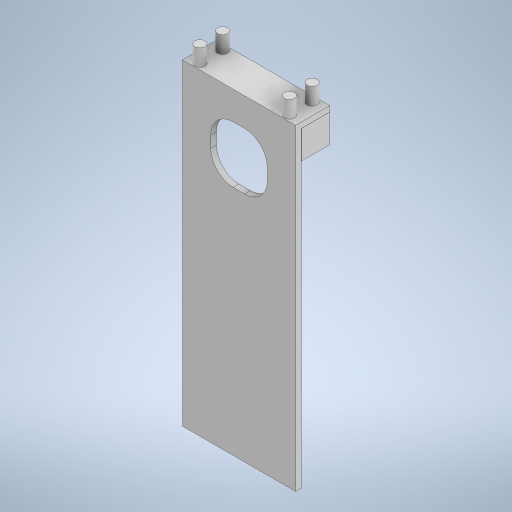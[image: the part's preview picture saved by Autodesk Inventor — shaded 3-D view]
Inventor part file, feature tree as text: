
AUTODESK INVENTOR PART (.ipt)
format: ipt  version: 2023 (Build 270158000, 158)  size: 316,928 bytes
history: native  units: mm
features: extrude x8, sketch x8
ambient origin geometry x8: Origin, YZ Plane, XZ Plane, XY Plane, X Axis, Y Axis, Z Axis, Center Point
bodies: Solid1 (feature_tree)
feature tree (16):
  extrude  "Extrusion1"  Depth=100.0mm
  extrude  "Extrusion6"  Depth=50.0mm
  sketch  "Sketch15"  dims[d22=50.0mm d23=20.0mm]
  sketch  "Sketch16"  dims[d24=5.0mm d25=0.0mm d46=100.0mm]
  extrude  "Extrusion11"  Depth=20.0mm
  extrude  "Extrusion12"  Depth=100.0mm
  extrude  "Extrusion13"  Depth=30.0mm
  extrude  "Extrusion14"  Depth=9.0mm
  extrude  "Extrusion16"  Depth=5.0mm TaperAngle=0.0deg
  extrude  "Extrusion17"  Depth=100.0mm
  sketch  "Sketch1"  dims[d0=100.0mm d1=200.0mm]
  sketch  "Sketch6"  dims[d2=5.0mm d3=0.0mm d21=50.0mm]
  sketch  "Sketch17"  dims[d47=30.0mm d48=9.0mm]
  sketch  "Sketch18"  dims[d49=9.0mm d50=9.0mm]
  sketch  "Sketch20"  dims[d51=9.0mm d52=5.0mm d53=0.0mm]
  sketch  "Sketch21"  dims[d54=15.0mm d55=0.0mm d56=100.0mm d57=30.0mm d58=5.0mm d59=0.0mm d60=5.0mm d61=0.0mm d64=5.0mm d65=0.0mm d66=100.0mm d67=80.0mm d68=5.0mm d69=0.0mm]
